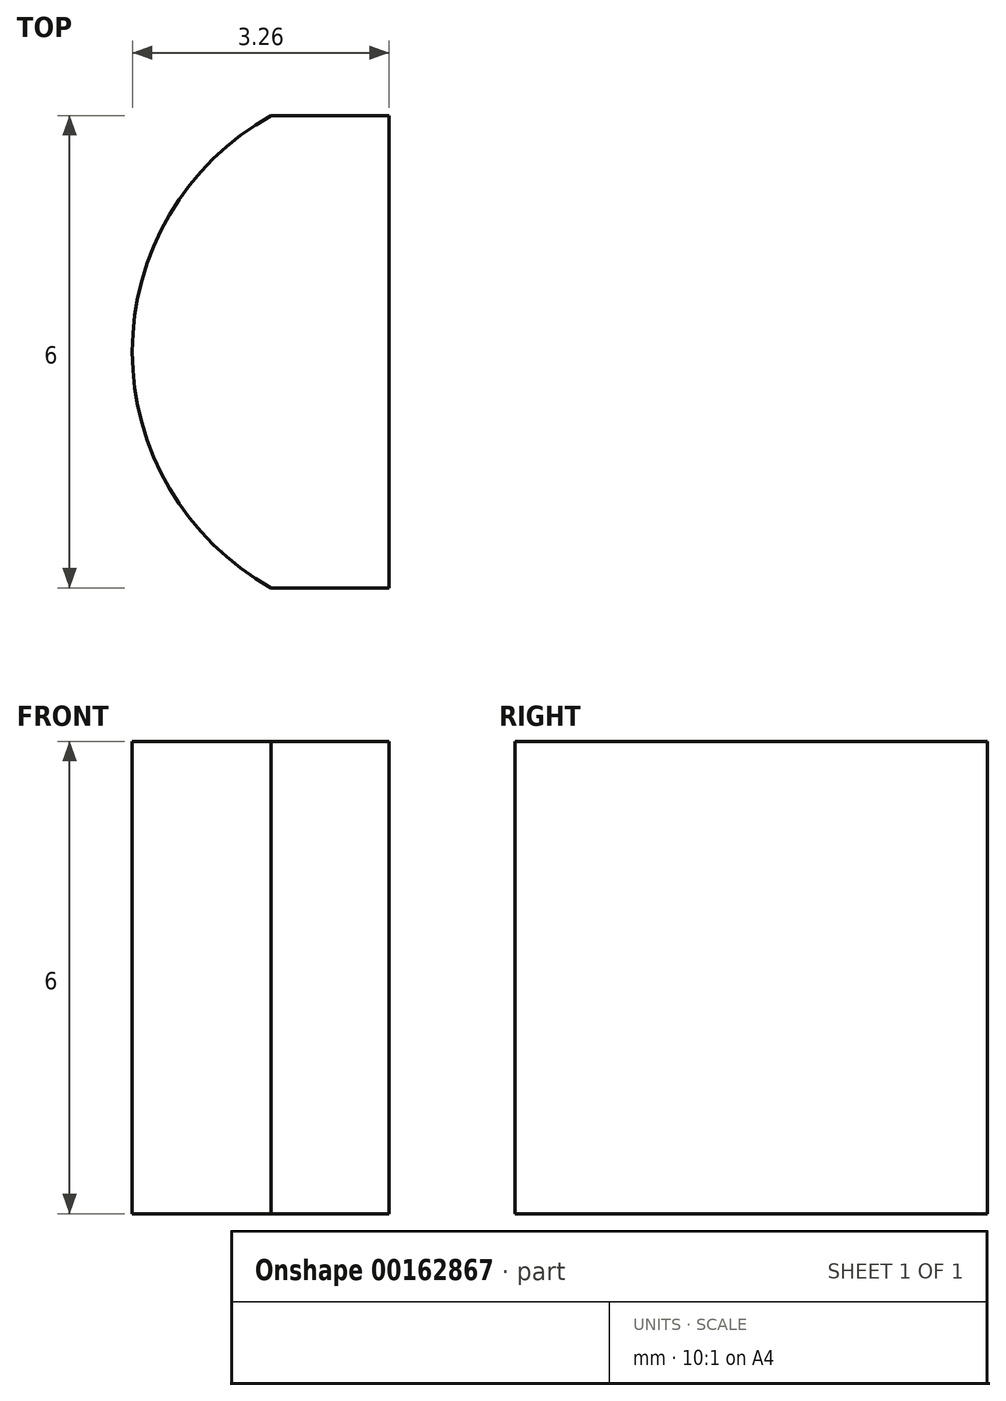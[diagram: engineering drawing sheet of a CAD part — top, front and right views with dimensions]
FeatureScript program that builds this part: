
annotation { "Feature Type Name" : "Feature", "Feature Type Description" : "" }
export const myFeature = defineFeature(function(context is Context, id is Id, definition is map)
    precondition{}
    {
        {
            assignVariable(context, id + "F0", {"name" : "d", "anyValue" : 6});
        }
        {
            var Q0;
            Q0=qCreatedBy(makeId("Top.planeOp"),FACE);
            var sketch = newSketch(context, id + "F1", { "sketchPlane" : qUnion([Q0])});
            skLineSegment(sketch, "E0.bottom", {"start": v(0, 3) * mm, "end": v(1.5, 3) * mm});
            skLineSegment(sketch, "E0.top", {"start": v(0, -3) * mm, "end": v(1.5, -3) * mm});
            skLineSegment(sketch, "E0.left", {"start": v(0, 3) * mm, "end": v(0, -3) * mm});
            skLineSegment(sketch, "E0.right", {"start": v(1.5, 3) * mm, "end": v(1.5, -3) * mm});
            skArc(sketch, "E1", {"start": v(0, 3) * mm, "mid": v(-1.76, 0) * mm, "end": v(0, -3) * mm});
            skLineSegment(sketch, "E2", {"start": v(-1.76, 3) * mm, "end": v(-1.76, -3) * mm, "construction": true});
            skPoint(sketch, "E3", {"position": v(7, 0) * mm});
            skSolve(sketch);
        }
        {
            var Q0;
            Q0 = qSketchRegion(id + "F1", true);
            extrude(context, id + "F2", {"entities" : qUnion([Q0]), "endBound" : BoundingType.SYMMETRIC, "depth" : (getVariable(context, 'd')) * mm});
        }
    });
